# Revit family: ВКП для круглих каналів_Eng
name_source: partatom
category: Mechanical Equipment
units: mm (PartAtom-declared; Revit-internal decimal feet)

## family parameters
Always vertical = Yes
Classification = None
Cut with Voids When Loaded = No
Part Type = Normal
Room Calculation Point = No
Round Connector Dimension = Use Diameter
Shared = No
Work Plane-Based = No

## types (7) — shared parameters
00_20_Manufacturer = Vents
00_20_Name = Inline centrifugal fan
Amperage = 0 A
Casing Material = Metal, painted, blue, matte RAL 5007
Description = For round ducts
Frequency = 50 Hz
H1 = 191 mm  [stored 0.62664 ft]
Load Classification = HVAC
Maintenance zone material = <By Category>
Manufacturer = Vents
Number of Fase = 1
URL = https://ventilation-system.com
Voltage = 230 V
zero-valued in all types: Default Elevation

## per-type parameters (varying)
- VKP 100: Apparent Load=60 VA; B=252 mm  [stored 0.826772 ft]; B1=80 mm; B2=129 mm  [stored 0.423228 ft]; Bottom=No; D=99 mm  [stored 0.324803 ft]; D1=99 mm  [stored 0.324803 ft]; D1y=94 mm  [stored 0.308399 ft]; Diameter=99 mm  [stored 0.324803 ft]; Double side=No; Dy=94 mm  [stored 0.308399 ft]; H=133 mm  [stored 0.436352 ft]; Height=133 mm  [stored 0.436352 ft]; L=420 mm  [stored 1.37795 ft]; L1=50 mm  [stored 0.164042 ft]; L11=99 mm  [stored 0.324803 ft]; L2=321 mm  [stored 1.05315 ft]; Length=420 mm  [stored 1.37795 ft]; Maximum Air Flow=240.0 m³/h; One side=Yes; Power=58 W; Sound pressure level at 3 m distance=47 dBA; Temperature of moving air=-25...+50 °С; Weight=4.65 kg; Width=252 mm  [stored 0.826772 ft]
- VKP 160: Apparent Load=87 VA; B=305 mm  [stored 1.00066 ft]; B1=110 mm; B2=189 mm  [stored 0.620079 ft]; Bottom=No; D=159 mm  [stored 0.521654 ft]; D1=159 mm  [stored 0.521654 ft]; D1y=154 mm  [stored 0.505249 ft]; Diameter=159 mm  [stored 0.521654 ft]; Double side=No; Dy=154 mm  [stored 0.505249 ft]; H=170 mm  [stored 0.557743 ft]; Height=170 mm  [stored 0.557743 ft]; L=480 mm  [stored 1.5748 ft]; L1=49 mm  [stored 0.160761 ft]; L11=98 mm; L2=382 mm  [stored 1.25328 ft]; Length=480 mm  [stored 1.5748 ft]; Maximum Air Flow=553.0 m³/h; One side=Yes; Power=85 W; Sound pressure level at 3 m distance=50 dBA; Temperature of moving air=-25...+40 °С; Weight=6.60 kg; Width=305 mm  [stored 1.00066 ft]
- VKP 125: Apparent Load=60 VA; B=252 mm  [stored 0.826772 ft]; B1=92 mm  [stored 0.301837 ft]; B2=154 mm  [stored 0.505249 ft]; Bottom=No; D=124 mm  [stored 0.406824 ft]; D1=124 mm  [stored 0.406824 ft]; D1y=119 mm  [stored 0.39042 ft]; Diameter=124 mm  [stored 0.406824 ft]; Double side=No; Dy=119 mm  [stored 0.39042 ft]; H=133 mm  [stored 0.436352 ft]; Height=133 mm  [stored 0.436352 ft]; L=420 mm  [stored 1.37795 ft]; L1=50 mm  [stored 0.164042 ft]; L11=99 mm  [stored 0.324803 ft]; L2=321 mm  [stored 1.05315 ft]; Length=420 mm  [stored 1.37795 ft]; Maximum Air Flow=340.0 m³/h; One side=Yes; Power=58 W; Sound pressure level at 3 m distance=48 dBA; Temperature of moving air=-25...+50 °С; Weight=4.55 kg; Width=252 mm  [stored 0.826772 ft]
- VKP 150: Apparent Load=87 VA; B=305 mm  [stored 1.00066 ft]; B1=105 mm  [stored 0.344488 ft]; B2=179 mm; Bottom=No; D=149 mm  [stored 0.488845 ft]; D1=149 mm  [stored 0.488845 ft]; D1y=144 mm  [stored 0.472441 ft]; Diameter=149 mm  [stored 0.488845 ft]; Double side=No; Dy=144 mm  [stored 0.472441 ft]; H=170 mm  [stored 0.557743 ft]; Height=170 mm  [stored 0.557743 ft]; L=480 mm  [stored 1.5748 ft]; L1=49 mm  [stored 0.160761 ft]; L11=98 mm; L2=382 mm  [stored 1.25328 ft]; Length=480 mm  [stored 1.5748 ft]; Maximum Air Flow=553.0 m³/h; One side=Yes; Power=85 W; Sound pressure level at 3 m distance=50 dBA; Temperature of moving air=-25...+40 °С; Weight=6.35 kg; Width=305 mm  [stored 1.00066 ft]
- VKP 125/100*2: Apparent Load=60 VA; B=252 mm  [stored 0.826772 ft]; B1=65 mm; B2=129 mm  [stored 0.423228 ft]; Bottom=No; D=124 mm  [stored 0.406824 ft]; D1=99 mm  [stored 0.324803 ft]; D1y=94 mm  [stored 0.308399 ft]; Diameter=124 mm  [stored 0.406824 ft]; Double side=Yes; Dy=119 mm  [stored 0.39042 ft]; H=133 mm  [stored 0.436352 ft]; Height=133 mm  [stored 0.436352 ft]; L=420 mm  [stored 1.37795 ft]; L1=50 mm  [stored 0.164042 ft]; L11=99 mm  [stored 0.324803 ft]; L2=321 mm  [stored 1.05315 ft]; Length=420 mm  [stored 1.37795 ft]; Maximum Air Flow=340.0 m³/h; One side=Yes; Power=58 W; Sound pressure level at 3 m distance=48 dBA; Temperature of moving air=-25...+50 °С; Weight=2.84 kg; Width=252 mm  [stored 0.826772 ft]
- VKP 125/100*4: Apparent Load=60 VA; B=252 mm  [stored 0.826772 ft]; B1=92 mm  [stored 0.301837 ft]; B2=129 mm  [stored 0.423228 ft]; Bottom=Yes; D=124 mm  [stored 0.406824 ft]; D1=99 mm  [stored 0.324803 ft]; D1y=94 mm  [stored 0.308399 ft]; Diameter=124 mm  [stored 0.406824 ft]; Double side=No; Dy=119 mm  [stored 0.39042 ft]; H=133 mm  [stored 0.436352 ft]; Height=191 mm  [stored 0.62664 ft]; L=376 mm  [stored 1.2336 ft]; L1=28 mm  [stored 0.0918635 ft]; L11=55 mm  [stored 0.180446 ft]; L2=321 mm  [stored 1.05315 ft]; Length=376 mm  [stored 1.2336 ft]; Maximum Air Flow=340.0 m³/h; One side=No; Power=58 W; Sound pressure level at 3 m distance=48 dBA; Temperature of moving air=-25...+50 °С; Weight=2.84 kg; Width=252 mm  [stored 0.826772 ft]
- VKP 150/125*2: Apparent Load=87 VA; B=300 mm; B1=77 mm  [stored 0.252625 ft]; B2=154 mm  [stored 0.505249 ft]; Bottom=No; D=149 mm  [stored 0.488845 ft]; D1=124 mm  [stored 0.406824 ft]; D1y=119 mm  [stored 0.39042 ft]; Diameter=149 mm  [stored 0.488845 ft]; Double side=Yes; Dy=144 mm  [stored 0.472441 ft]; H=170 mm  [stored 0.557743 ft]; Height=170 mm  [stored 0.557743 ft]; L=480 mm  [stored 1.5748 ft]; L1=49 mm  [stored 0.160761 ft]; L11=98 mm; L2=382 mm  [stored 1.25328 ft]; Length=480 mm  [stored 1.5748 ft]; Maximum Air Flow=553.0 m³/h; One side=Yes; Power=85 W; Sound pressure level at 3 m distance=50 dBA; Temperature of moving air=-25...+40 °С; Weight=6.33 kg; Width=300 mm

note: column(s) folded — value = type name in every type: 00_20_Type

note: [stored X ft] marks values corroborated as IEEE doubles in the binary element streams (Revit-internal decimal feet)
